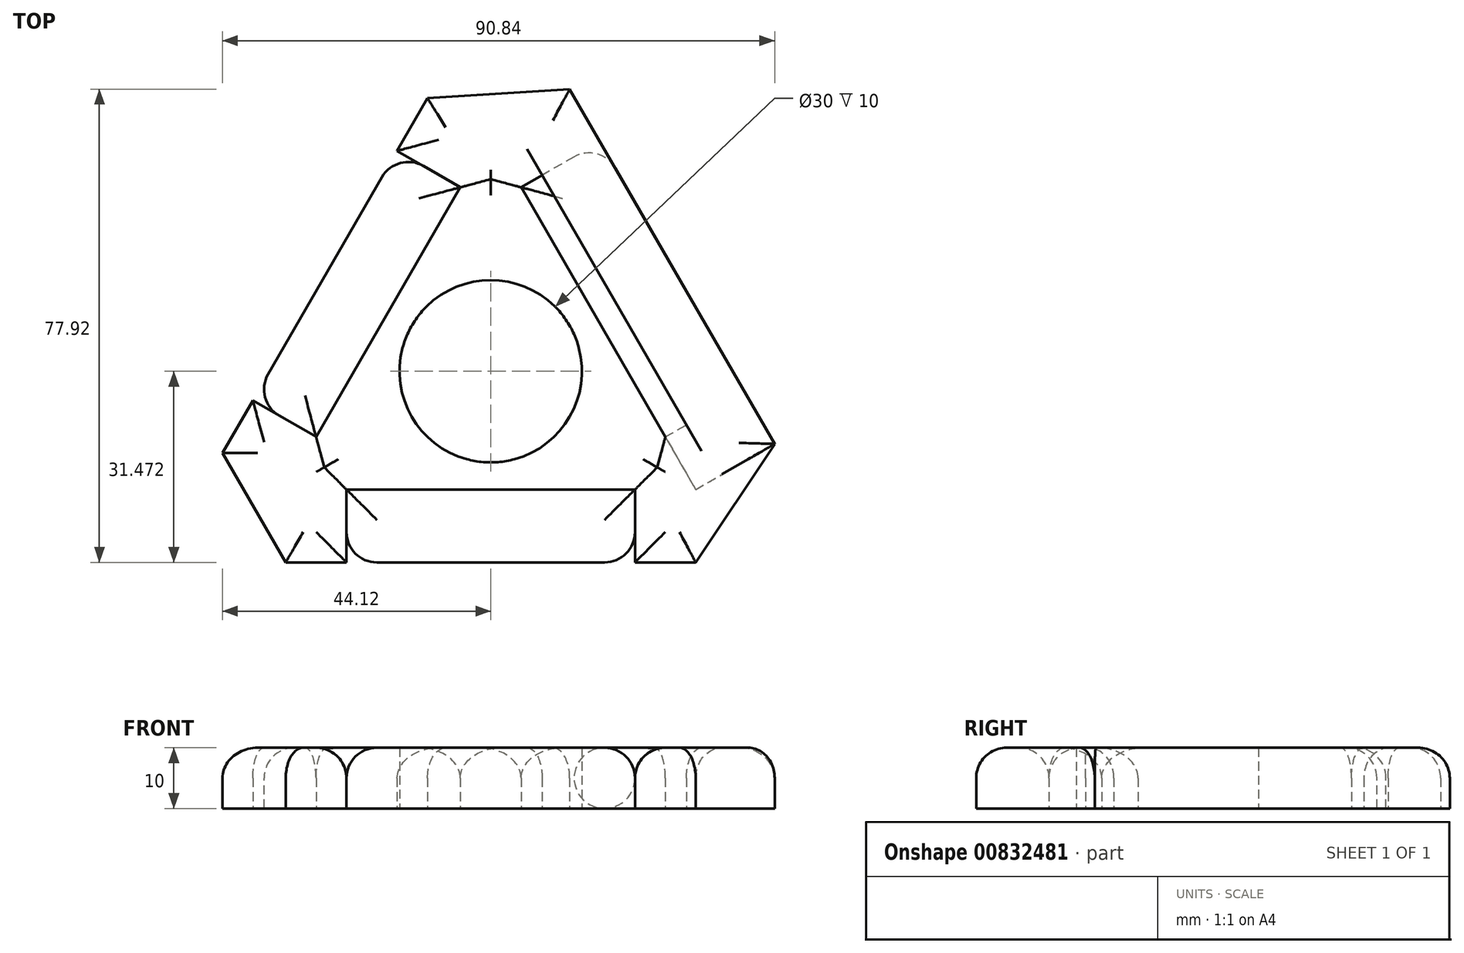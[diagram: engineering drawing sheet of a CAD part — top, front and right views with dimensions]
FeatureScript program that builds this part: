
annotation { "Feature Type Name" : "Feature", "Feature Type Description" : "" }
export const myFeature = defineFeature(function(context is Context, id is Id, definition is map)
    precondition{}
    {
        {
            var Q0;
            Q0=qCreatedBy(makeId("Top.planeOp"),FACE);
            var sketch = newSketch(context, id + "F0", { "sketchPlane" : qUnion([Q0])});
            skLineSegment(sketch, "E0", {"start": v(-33.73, 0) * mm, "end": v(0, 58.42) * mm});
            skLineSegment(sketch, "E1", {"start": v(0, 58.42) * mm, "end": v(33.73, 0) * mm});
            skLineSegment(sketch, "E2", {"start": v(33.73, 0) * mm, "end": v(-33.73, 0) * mm});
            skLineSegment(sketch, "E3.0", {"start": v(13, 65.92) * mm, "end": v(46.72, 7.5) * mm});
            skLineSegment(sketch, "E4", {"start": v(0, 58.42) * mm, "end": v(13, 65.92) * mm});
            skLineSegment(sketch, "E5", {"start": v(33.73, 0) * mm, "end": v(46.72, 7.5) * mm});
            skLineSegment(sketch, "E6.0", {"start": v(33.73, -12) * mm, "end": v(-33.73, -12) * mm});
            skLineSegment(sketch, "E7.0", {"start": v(-44.12, 6) * mm, "end": v(-10.4, 64.42) * mm});
            skLineSegment(sketch, "E8", {"start": v(-10.4, 64.42) * mm, "end": v(0, 58.42) * mm});
            skLineSegment(sketch, "E9", {"start": v(-44.12, 6) * mm, "end": v(-33.73, 0) * mm});
            skLineSegment(sketch, "E10", {"start": v(-33.73, 0) * mm, "end": v(-33.73, -12) * mm});
            skLineSegment(sketch, "E11", {"start": v(33.73, 0) * mm, "end": v(33.73, -12) * mm});
            skLineSegment(sketch, "E12", {"start": v(-10.4, 64.42) * mm, "end": v(13, 65.92) * mm});
            skLineSegment(sketch, "E13", {"start": v(46.72, 7.5) * mm, "end": v(33.73, -12) * mm});
            skLineSegment(sketch, "E14", {"start": v(-44.12, 6) * mm, "end": v(-33.73, -12) * mm});
            skLineSegment(sketch, "E15", {"start": v(18, 57.26) * mm, "end": v(5, 49.76) * mm});
            skLineSegment(sketch, "E16.0", {"start": v(28.73, 8.66) * mm, "end": v(39.12, 14.66) * mm});
            skLineSegment(sketch, "E17", {"start": v(8.46, 51.76) * mm, "end": v(32.2, 10.66) * mm});
            skLineSegment(sketch, "E18", {"start": v(-16.86, 29.2) * mm, "end": v(0, 19.47) * mm});
            skLineSegment(sketch, "E19", {"start": v(0, 19.47) * mm, "end": v(16.86, 29.2) * mm});
            skLineSegment(sketch, "E20.1.0", {"start": v(-41.72, 16.16) * mm, "end": v(-28.73, 8.66) * mm});
            skLineSegment(sketch, "E20.1.1", {"start": v(-32.2, 10.66) * mm, "end": v(-8.46, 51.76) * mm});
            skLineSegment(sketch, "E20.1.2", {"start": v(-5, 49.76) * mm, "end": v(-15.4, 55.76) * mm});
            skLineSegment(sketch, "E20.2.0", {"start": v(23.73, -15) * mm, "end": v(23.73, 0) * mm});
            skLineSegment(sketch, "E20.2.1", {"start": v(23.73, -4) * mm, "end": v(-23.73, -4) * mm});
            skLineSegment(sketch, "E20.2.2", {"start": v(-23.73, 0) * mm, "end": v(-23.73, -12) * mm});
            skPoint(sketch, "E20.center", {"position": v(0, 19.47) * mm});
            skCircle(sketch, "E21", {"center": v(0, 19.47) * mm, "radius": 15 * mm});
            skSolve(sketch);
        }
        {
            var Q0;
            {var subQ4=sQuery(id+"F0.wireOp",EDGE,"E10");Q0=makeQuery(id+"F0.imprint","IMPRINT",FACE,{"disambiguationData":[TD([[makeQuery(id+"F0.imprint","IMPRINT",EDGE,{"derivedFrom":subQ4}),1.0]])]});}
            var Q1;
            {var subQ0=sQuery(id+"F0.wireOp",EDGE,"E11");Q1=makeQuery(id+"F0.imprint","IMPRINT",FACE,{"disambiguationData":[TD([[makeQuery(id+"F0.imprint","IMPRINT",EDGE,{"derivedFrom":subQ0}),-1.0]])]});}
            var Q2;
            Q2=makeQuery(id+"F0.imprint","IMPRINT",FACE,{"disambiguationData":[TD([[makeQuery(id+"F0.imprint","IMPRINT",EDGE,{"derivedFrom":sQuery(id+"F0.wireOp",EDGE,"E5")}),-1.0]])]});
            var Q3;
            {var subQ4=sQuery(id+"F0.wireOp",EDGE,"E5");Q3=makeQuery(id+"F0.imprint","IMPRINT",FACE,{"disambiguationData":[TD([[makeQuery(id+"F0.imprint","IMPRINT",EDGE,{"derivedFrom":subQ4}),1.0]])]});}
            var Q4;
            {var subQ0=sQuery(id+"F0.wireOp",EDGE,"E4");Q4=makeQuery(id+"F0.imprint","IMPRINT",FACE,{"disambiguationData":[TD([[makeQuery(id+"F0.imprint","IMPRINT",EDGE,{"derivedFrom":subQ0}),-1.0]])]});}
            var Q5;
            Q5=makeQuery(id+"F0.imprint","IMPRINT",FACE,{"disambiguationData":[TD([[makeQuery(id+"F0.imprint","IMPRINT",EDGE,{"derivedFrom":sQuery(id+"F0.wireOp",EDGE,"E4")}),1.0]])]});
            var Q6;
            {var subQ4=sQuery(id+"F0.wireOp",EDGE,"E8");Q6=makeQuery(id+"F0.imprint","IMPRINT",FACE,{"disambiguationData":[TD([[makeQuery(id+"F0.imprint","IMPRINT",EDGE,{"derivedFrom":subQ4}),-1.0]])]});}
            var Q7;
            {var subQ4=sQuery(id+"F0.wireOp",EDGE,"E9");Q7=makeQuery(id+"F0.imprint","IMPRINT",FACE,{"disambiguationData":[TD([[makeQuery(id+"F0.imprint","IMPRINT",EDGE,{"derivedFrom":subQ4}),1.0]])]});}
            var Q8;
            Q8=makeQuery(id+"F0.imprint","IMPRINT",FACE,{"disambiguationData":[TD([[makeQuery(id+"F0.imprint","IMPRINT",EDGE,{"derivedFrom":sQuery(id+"F0.wireOp",EDGE,"E9")}),-1.0]])]});
            var Q9;
            {var subQ4=sQuery(id+"F0.wireOp",EDGE,"E0");var subQ8=sQuery(id+"F0.wireOp",EDGE,"E18");var subQ11=makeQuery(id+"F0.imprint","INTERSECT",VERTEX,{"derivedFrom":[subQ4,subQ8]});Q9=makeQuery(id+"F0.imprint","IMPRINT",FACE,{"disambiguationData":[TD([[makeQuery(id+"F0.imprint","IMPRINT",EDGE,{"disambiguationData":[TD([[subQ11,-1.0]])],"derivedFrom":subQ4}),-1.0]])]});}
            var Q10;
            {var subQ6=sQuery(id+"F0.wireOp",EDGE,"E18");var subQ7=sQuery(id+"F0.wireOp",EDGE,"E0");var subQ8=makeQuery(id+"F0.imprint","INTERSECT",VERTEX,{"derivedFrom":[subQ7,subQ6]});Q10=makeQuery(id+"F0.imprint","IMPRINT",FACE,{"disambiguationData":[TD([[makeQuery(id+"F0.imprint","IMPRINT",EDGE,{"disambiguationData":[TD([[subQ8,1.0]])],"derivedFrom":subQ7}),-1.0]])]});}
            extrude(context, id + "F1", {"entities" : qUnion([Q0, Q1, Q2, Q3, Q4, Q5, Q6, Q7, Q8, Q9, Q10]), "depth" : 10 * mm, "offsetDistance" : 25 * mm});
        }
        {
            var Q0;
            {var subQ3=sQuery(id+"F0.wireOp",EDGE,"E17");Q0=makeQuery(id+"F0.imprint","IMPRINT",FACE,{"disambiguationData":[TD([[makeQuery(id+"F0.imprint","IMPRINT",EDGE,{"derivedFrom":subQ3}),-1.0]])]});}
            var Q1;
            {var subQ5=sQuery(id+"F0.wireOp",EDGE,"E17");Q1=makeQuery(id+"F0.imprint","IMPRINT",FACE,{"disambiguationData":[TD([[makeQuery(id+"F0.imprint","IMPRINT",EDGE,{"derivedFrom":subQ5}),1.0]])]});}
            extrude(context, id + "F2", {"entities" : qUnion([Q0, Q1]), "depth" : 10 * mm, "offsetDistance" : 25 * mm});
        }
        {
            var Q0;
            {var subQ0=sQuery(id+"F0.wireOp",EDGE,"E20.1.1");Q0=makeQuery(id+"F0.imprint","IMPRINT",FACE,{"disambiguationData":[TD([[makeQuery(id+"F0.imprint","IMPRINT",EDGE,{"derivedFrom":subQ0}),-1.0]])]});}
            var Q1;
            {var subQ5=sQuery(id+"F0.wireOp",EDGE,"E20.1.1");Q1=makeQuery(id+"F0.imprint","IMPRINT",FACE,{"disambiguationData":[TD([[makeQuery(id+"F0.imprint","IMPRINT",EDGE,{"derivedFrom":subQ5}),1.0]])]});}
            extrude(context, id + "F3", {"entities" : qUnion([Q0, Q1]), "depth" : 10 * mm, "offsetDistance" : 25 * mm});
        }
        {
            var Q0;
            {var subQ5=sQuery(id+"F0.wireOp",EDGE,"E20.2.1");Q0=makeQuery(id+"F0.imprint","IMPRINT",FACE,{"disambiguationData":[TD([[makeQuery(id+"F0.imprint","IMPRINT",EDGE,{"derivedFrom":subQ5}),-1.0]])]});}
            var Q1;
            {var subQ5=sQuery(id+"F0.wireOp",EDGE,"E20.2.1");Q1=makeQuery(id+"F0.imprint","IMPRINT",FACE,{"disambiguationData":[TD([[makeQuery(id+"F0.imprint","IMPRINT",EDGE,{"derivedFrom":subQ5}),1.0]])]});}
            extrude(context, id + "F4", {"entities" : qUnion([Q0, Q1]), "depth" : 10 * mm, "offsetDistance" : 25 * mm});
        }
        {
            var Q0;
            Q0=makeQuery(id+"F3.opExtrude","CAP_EDGE",EDGE,{"disambiguationData":[OSD([sQuery(id+"F0.wireOp",EDGE,"E0")])],"isStart":false});
            var Q1;
            Q1=makeQuery(id+"F2.opExtrude","CAP_EDGE",EDGE,{"disambiguationData":[OSD([sQuery(id+"F0.wireOp",EDGE,"E1")])],"isStart":false});
            var Q2;
            Q2=makeQuery(id+"F4.opExtrude","CAP_EDGE",EDGE,{"disambiguationData":[OSD([sQuery(id+"F0.wireOp",EDGE,"E2")])],"isStart":false});
            var Q3;
            Q3=makeQuery(id+"F4.opExtrude","SWEPT_EDGE",EDGE,{"disambiguationData":[OSD([sQuery(id+"F0.wireOp",EDGE,"E6.0"),sQuery(id+"F0.wireOp",EDGE,"E20.2.0")])]});
            var Q4;
            Q4=makeQuery(id+"F4.opExtrude","SWEPT_EDGE",EDGE,{"disambiguationData":[OSD([sQuery(id+"F0.wireOp",EDGE,"E6.0"),sQuery(id+"F0.wireOp",EDGE,"E20.2.2")])]});
            var Q5;
            Q5=makeQuery(id+"F2.opExtrude","SWEPT_EDGE",EDGE,{"disambiguationData":[OSD([sQuery(id+"F0.wireOp",EDGE,"E3.0"),sQuery(id+"F0.wireOp",EDGE,"E16.0")])]});
            var Q6;
            Q6=makeQuery(id+"F2.opExtrude","SWEPT_EDGE",EDGE,{"disambiguationData":[OSD([sQuery(id+"F0.wireOp",EDGE,"E3.0"),sQuery(id+"F0.wireOp",EDGE,"E15")])]});
            var Q7;
            Q7=makeQuery(id+"F3.opExtrude","SWEPT_EDGE",EDGE,{"disambiguationData":[OSD([sQuery(id+"F0.wireOp",EDGE,"E7.0"),sQuery(id+"F0.wireOp",EDGE,"E20.1.2")])]});
            var Q8;
            Q8=makeQuery(id+"F3.opExtrude","SWEPT_EDGE",EDGE,{"disambiguationData":[OSD([sQuery(id+"F0.wireOp",EDGE,"E7.0"),sQuery(id+"F0.wireOp",EDGE,"E20.1.0")])]});
            var Q9;
            Q9=makeQuery(id+"F4.opExtrude","CAP_EDGE",EDGE,{"disambiguationData":[OSD([sQuery(id+"F0.wireOp",EDGE,"E6.0")])],"isStart":false});
            var Q10;
            Q10=makeQuery(id+"F2.opExtrude","CAP_EDGE",EDGE,{"disambiguationData":[OSD([sQuery(id+"F0.wireOp",EDGE,"E3.0")])],"isStart":false});
            var Q11;
            Q11=makeQuery(id+"F3.opExtrude","CAP_FACE",FACE,{"disambiguationData":[OSD([sQuery(id+"F0.wireOp",EDGE,"E0"),sQuery(id+"F0.wireOp",EDGE,"E7.0"),sQuery(id+"F0.wireOp",EDGE,"E20.1.0"),sQuery(id+"F0.wireOp",EDGE,"E20.1.2")])],"isStart":false});
            var Q12;
            Q12=makeQuery(id+"F4.opExtrude","CAP_EDGE",EDGE,{"disambiguationData":[OSD([sQuery(id+"F0.wireOp",EDGE,"E20.2.0")])],"isStart":false});
            var Q13;
            Q13=makeQuery(id+"F4.opExtrude","CAP_EDGE",EDGE,{"disambiguationData":[OSD([sQuery(id+"F0.wireOp",EDGE,"E20.2.2")])],"isStart":false});
            var Q14;
            Q14=makeQuery(id+"F2.opExtrude","CAP_EDGE",EDGE,{"disambiguationData":[OSD([sQuery(id+"F0.wireOp",EDGE,"E16.0")])],"isStart":false});
            var Q15;
            Q15=makeQuery(id+"F2.opExtrude","CAP_EDGE",EDGE,{"disambiguationData":[OSD([sQuery(id+"F0.wireOp",EDGE,"E15")])],"isStart":false});
            fillet(context, id + "F5", {"entities" : qUnion([Q0, Q1, Q2, Q3, Q4, Q5, Q6, Q7, Q8, Q9, Q10, Q11, Q12, Q13, Q14, Q15]), "radius" : 5 * mm, "tangentPropagation" : true, "allowEdgeOverflow" : false});
        }
        {
            var Q0;
            Q0=makeQuery(id+"F1.opExtrude","CAP_EDGE",EDGE,{"disambiguationData":[OSD([sQuery(id+"F0.wireOp",EDGE,"E0")])],"isStart":false});
            var Q1;
            Q1=makeQuery(id+"F1.opExtrude","CAP_EDGE",EDGE,{"disambiguationData":[OSD([sQuery(id+"F0.wireOp",EDGE,"E1")])],"isStart":false});
            var Q2;
            Q2=makeQuery(id+"F1.opExtrude","CAP_EDGE",EDGE,{"disambiguationData":[OSD([sQuery(id+"F0.wireOp",EDGE,"E2")])],"isStart":false});
            var Q3;
            Q3=makeQuery(id+"F1.opExtrude","CAP_EDGE",EDGE,{"disambiguationData":[OSD([sQuery(id+"F0.wireOp",EDGE,"E15")])],"isStart":false});
            var Q4;
            Q4=makeQuery(id+"F1.opExtrude","CAP_EDGE",EDGE,{"disambiguationData":[OSD([sQuery(id+"F0.wireOp",EDGE,"E20.1.2")])],"isStart":false});
            var Q5;
            Q5=makeQuery(id+"F1.opExtrude","CAP_EDGE",EDGE,{"disambiguationData":[OSD([sQuery(id+"F0.wireOp",EDGE,"E20.1.0")])],"isStart":false});
            var Q6;
            Q6=makeQuery(id+"F1.opExtrude","CAP_EDGE",EDGE,{"disambiguationData":[OSD([sQuery(id+"F0.wireOp",EDGE,"E20.2.2")])],"isStart":false});
            var Q7;
            Q7=makeQuery(id+"F1.opExtrude","CAP_EDGE",EDGE,{"disambiguationData":[OSD([sQuery(id+"F0.wireOp",EDGE,"E20.2.0")])],"isStart":false});
            var Q8;
            Q8=makeQuery(id+"F1.opExtrude","CAP_EDGE",EDGE,{"disambiguationData":[OSD([sQuery(id+"F0.wireOp",EDGE,"E16.0")])],"isStart":false});
            var Q9;
            Q9=makeQuery(id+"F1.opExtrude","CAP_EDGE",EDGE,{"disambiguationData":[OSD([sQuery(id+"F0.wireOp",EDGE,"E14")])],"isStart":false});
            var Q10;
            Q10=makeQuery(id+"F1.opExtrude","CAP_EDGE",EDGE,{"disambiguationData":[OSD([sQuery(id+"F0.wireOp",EDGE,"E13")])],"isStart":false});
            var Q11;
            Q11=makeQuery(id+"F1.opExtrude","CAP_EDGE",EDGE,{"disambiguationData":[OSD([sQuery(id+"F0.wireOp",EDGE,"E12")])],"isStart":false});
            var Q12;
            {var subQ0=sQuery(id+"F0.wireOp",EDGE,"E3.0");Q12=makeQuery(id+"F1.opExtrude","CAP_EDGE",EDGE,{"disambiguationData":[OSD([subQ0]),TDD([makeQuery(id+"F0.imprint","IMPRINT",EDGE,{"disambiguationData":[TD([[makeQuery(id+"F0.imprint","INTERSECT",VERTEX,{"derivedFrom":[subQ0,sQuery(id+"F0.wireOp",EDGE,"E16.0")]}),-1.0]])],"derivedFrom":subQ0})])],"isStart":false});}
            var Q13;
            {var subQ0=sQuery(id+"F0.wireOp",EDGE,"E6.0");Q13=makeQuery(id+"F1.opExtrude","CAP_EDGE",EDGE,{"disambiguationData":[OSD([subQ0]),TDD([makeQuery(id+"F0.imprint","IMPRINT",EDGE,{"disambiguationData":[TD([[makeQuery(id+"F0.imprint","INTERSECT",VERTEX,{"derivedFrom":[subQ0,sQuery(id+"F0.wireOp",EDGE,"E20.2.0")]}),1.0]])],"derivedFrom":subQ0})])],"isStart":false});}
            var Q14;
            {var subQ0=sQuery(id+"F0.wireOp",EDGE,"E3.0");Q14=makeQuery(id+"F1.opExtrude","CAP_EDGE",EDGE,{"disambiguationData":[OSD([subQ0]),TDD([makeQuery(id+"F0.imprint","IMPRINT",EDGE,{"disambiguationData":[TD([[makeQuery(id+"F0.imprint","INTERSECT",VERTEX,{"derivedFrom":[subQ0,sQuery(id+"F0.wireOp",EDGE,"E15")]}),1.0]])],"derivedFrom":subQ0})])],"isStart":false});}
            var Q15;
            {var subQ0=sQuery(id+"F0.wireOp",EDGE,"E7.0");Q15=makeQuery(id+"F1.opExtrude","CAP_EDGE",EDGE,{"disambiguationData":[OSD([subQ0]),TDD([makeQuery(id+"F0.imprint","IMPRINT",EDGE,{"disambiguationData":[TD([[makeQuery(id+"F0.imprint","INTERSECT",VERTEX,{"derivedFrom":[subQ0,sQuery(id+"F0.wireOp",EDGE,"E20.1.2")]}),-1.0]])],"derivedFrom":subQ0})])],"isStart":false});}
            var Q16;
            {var subQ0=sQuery(id+"F0.wireOp",EDGE,"E7.0");Q16=makeQuery(id+"F1.opExtrude","CAP_EDGE",EDGE,{"disambiguationData":[OSD([subQ0]),TDD([makeQuery(id+"F0.imprint","IMPRINT",EDGE,{"disambiguationData":[TD([[makeQuery(id+"F0.imprint","INTERSECT",VERTEX,{"derivedFrom":[subQ0,sQuery(id+"F0.wireOp",EDGE,"E20.1.0")]}),1.0]])],"derivedFrom":subQ0})])],"isStart":false});}
            var Q17;
            {var subQ0=sQuery(id+"F0.wireOp",EDGE,"E6.0");Q17=makeQuery(id+"F1.opExtrude","CAP_EDGE",EDGE,{"disambiguationData":[OSD([subQ0]),TDD([makeQuery(id+"F0.imprint","IMPRINT",EDGE,{"disambiguationData":[TD([[makeQuery(id+"F0.imprint","INTERSECT",VERTEX,{"derivedFrom":[subQ0,sQuery(id+"F0.wireOp",EDGE,"E20.2.2")]}),-1.0]])],"derivedFrom":subQ0})])],"isStart":false});}
            fillet(context, id + "F6", {"entities" : qUnion([Q0, Q1, Q2, Q3, Q4, Q5, Q6, Q7, Q8, Q9, Q10, Q11, Q12, Q13, Q14, Q15, Q16, Q17]), "radius" : 5 * mm, "tangentPropagation" : true, "allowEdgeOverflow" : false});
        }
    });
